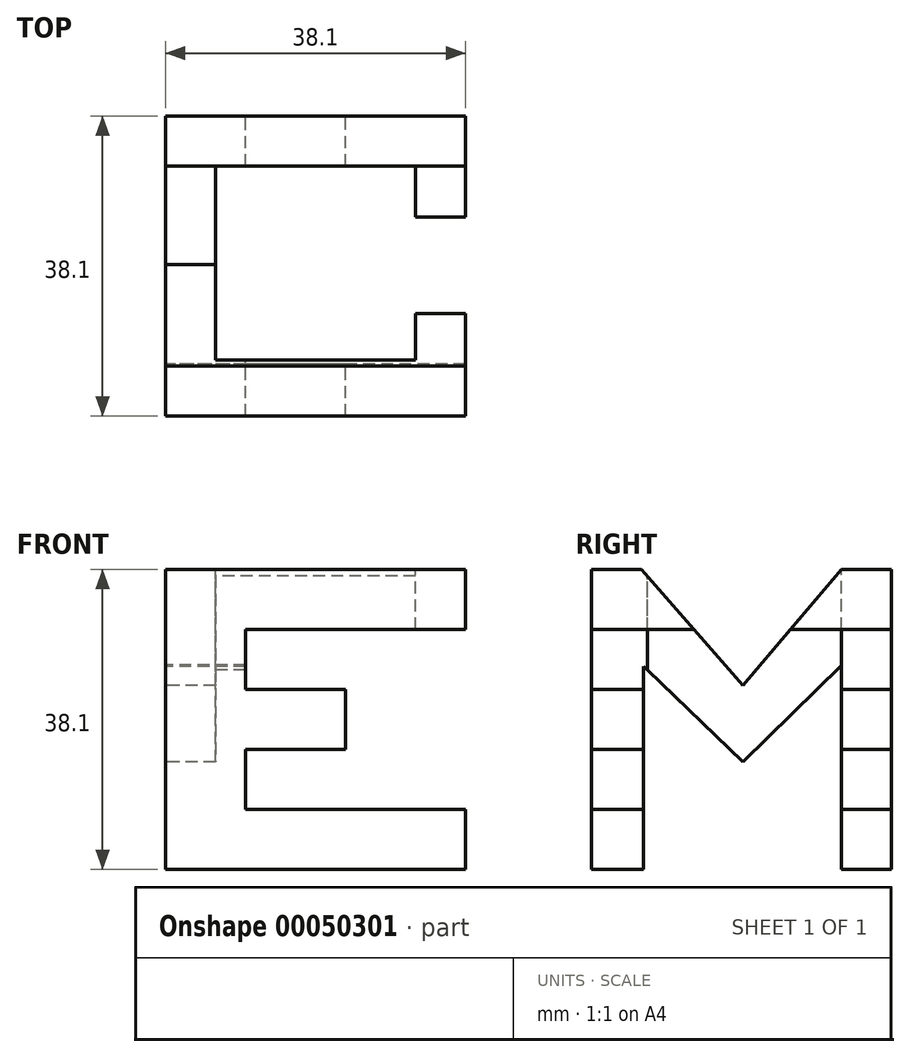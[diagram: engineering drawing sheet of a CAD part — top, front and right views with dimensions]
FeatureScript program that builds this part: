
annotation { "Feature Type Name" : "Feature", "Feature Type Description" : "" }
export const myFeature = defineFeature(function(context is Context, id is Id, definition is map)
    precondition{}
    {
        {
            var Q0;
            Q0=qCreatedBy(makeId("Front.planeOp"),FACE);
            var sketch = newSketch(context, id + "F0", { "sketchPlane" : qUnion([Q0])});
            skLineSegment(sketch, "E0.bottom", {"start": v(0, 0) * mm, "end": v(38.1, 0) * mm});
            skLineSegment(sketch, "E0.top", {"start": v(0, 38.1) * mm, "end": v(38.1, 38.1) * mm});
            skLineSegment(sketch, "E0.left", {"start": v(0, 0) * mm, "end": v(0, 38.1) * mm});
            skLineSegment(sketch, "E0.right", {"start": v(38.1, 0) * mm, "end": v(38.1, 38.1) * mm});
            skSolve(sketch);
        }
        {
            var Q0;
            Q0=qCreatedBy(makeId("Front.planeOp"),FACE);
            var sketch = newSketch(context, id + "F1", { "sketchPlane" : qUnion([Q0])});
            skSolve(sketch);
        }
        {
            var Q0;
            Q0 = qSketchRegion(id + "F1", true);
            var Q1;
            Q1=makeQuery(id+"F0.imprint","IMPRINT",FACE,{"disambiguationData":[TD([[makeQuery(id+"F0.imprint","IMPRINT",EDGE,{"derivedFrom":sQuery(id+"F0.wireOp",EDGE,"E0.bottom")}),1.0]])]});
            extrude(context, id + "F2", {"entities" : qUnion([Q0, Q1]), "depth" : 38.1 * mm});
        }
        {
            var Q0;
            Q0=qCreatedBy(makeId("Front.planeOp"),FACE);
            var sketch = newSketch(context, id + "F3", { "sketchPlane" : qUnion([Q0])});
            skLineSegment(sketch, "E1", {"start": v(0, 0) * mm, "end": v(0, 38.1) * mm});
            skLineSegment(sketch, "E2", {"start": v(0, 38.1) * mm, "end": v(38.1, 38.1) * mm});
            skLineSegment(sketch, "E3", {"start": v(38.1, 38.1) * mm, "end": v(38.1, 30.48) * mm});
            skLineSegment(sketch, "E4", {"start": v(38.1, 30.48) * mm, "end": v(10.16, 30.48) * mm});
            skLineSegment(sketch, "E5", {"start": v(10.16, 30.48) * mm, "end": v(10.16, 22.86) * mm});
            skLineSegment(sketch, "E6", {"start": v(10.16, 22.86) * mm, "end": v(22.86, 22.86) * mm});
            skLineSegment(sketch, "E7", {"start": v(22.86, 22.86) * mm, "end": v(22.86, 15.24) * mm});
            skLineSegment(sketch, "E8", {"start": v(22.86, 15.24) * mm, "end": v(10.16, 15.24) * mm});
            skLineSegment(sketch, "E9", {"start": v(10.16, 15.24) * mm, "end": v(10.16, 7.62) * mm});
            skLineSegment(sketch, "E10", {"start": v(10.16, 7.62) * mm, "end": v(38.1, 7.62) * mm});
            skLineSegment(sketch, "E11", {"start": v(38.1, 7.62) * mm, "end": v(38.1, 0) * mm});
            skLineSegment(sketch, "E12", {"start": v(38.1, 7.62) * mm, "end": v(38.1, 30.48) * mm});
            skSolve(sketch);
        }
        {
            var Q0;
            Q0=makeQuery(id+"F3.imprint","IMPRINT",FACE,{"disambiguationData":[TD([[makeQuery(id+"F3.imprint","IMPRINT",EDGE,{"derivedFrom":sQuery(id+"F3.wireOp",EDGE,"E4")}),1.0]])]});
            extrude(context, id + "F4", {"entities" : qUnion([Q0]), "operationType" : NewBodyOperationType.REMOVE, "depth" : 38.1 * mm});
        }
        {
            var Q0;
            Q0=qCreatedBy(makeId("Top.planeOp"),FACE);
            cPlane(context, id + "F5", {"entities" : qUnion([Q0]), "cplaneType" : CPlaneType.OFFSET, "offset" : 38.1 * mm, "width" : 152.4 * mm, "height" : 152.4 * mm});
        }
        {
            var Q0;
            Q0=qCreatedBy(id+"F5.planeOp",FACE);
            var sketch = newSketch(context, id + "F6", { "sketchPlane" : qUnion([Q0])});
            skLineSegment(sketch, "E13", {"start": v(0, 0) * mm, "end": v(0, -38.1) * mm});
            skLineSegment(sketch, "E14", {"start": v(0, -38.1) * mm, "end": v(38.1, -38.1) * mm});
            skLineSegment(sketch, "E15", {"start": v(38.1, -38.1) * mm, "end": v(38.1, 0) * mm});
            skLineSegment(sketch, "E16", {"start": v(0, 0) * mm, "end": v(38.1, 0) * mm});
            skLineSegment(sketch, "E17", {"start": v(6.35, -6.38) * mm, "end": v(31.75, -6.38) * mm});
            skLineSegment(sketch, "E18", {"start": v(31.75, -6.38) * mm, "end": v(31.75, -31.02) * mm});
            skLineSegment(sketch, "E19", {"start": v(31.75, -31.02) * mm, "end": v(6.35, -31.02) * mm});
            skLineSegment(sketch, "E20", {"start": v(6.35, -31.02) * mm, "end": v(6.35, -6.38) * mm});
            skSolve(sketch);
        }
        {
            var Q0;
            Q0=qCreatedBy(id+"F5.planeOp",FACE);
            var sketch = newSketch(context, id + "F7", { "sketchPlane" : qUnion([Q0])});
            skSolve(sketch);
        }
        {
            var Q0;
            Q0 = qSketchRegion(id + "F7", true);
            var Q1;
            Q1=makeQuery(id+"F6.imprint","IMPRINT",FACE,{"disambiguationData":[TD([[makeQuery(id+"F6.imprint","IMPRINT",EDGE,{"derivedFrom":sQuery(id+"F6.wireOp",EDGE,"E17")}),-1.0]])]});
            extrude(context, id + "F8", {"entities" : qUnion([Q0, Q1]), "operationType" : NewBodyOperationType.REMOVE, "oppositeDirection" : true, "depth" : 38.1 * mm});
        }
        {
            var Q0;
            Q0=qCreatedBy(makeId("Right.planeOp"),FACE);
            var sketch = newSketch(context, id + "F9", { "sketchPlane" : qUnion([Q0])});
            skLineSegment(sketch, "E21", {"start": v(0, 0) * mm, "end": v(-6.35, 0) * mm});
            skLineSegment(sketch, "E22", {"start": v(-6.35, 0) * mm, "end": v(-6.35, 21.6) * mm});
            skLineSegment(sketch, "E23", {"start": v(-6.35, 21.6) * mm, "end": v(-18.86, 10.86) * mm});
            skLineSegment(sketch, "E24", {"start": v(-18.86, 10.86) * mm, "end": v(-31.78, 21.63) * mm});
            skLineSegment(sketch, "E25", {"start": v(-31.78, 21.63) * mm, "end": v(-31.78, 0) * mm});
            skLineSegment(sketch, "E26", {"start": v(-6.35, 38.1) * mm, "end": v(-18.86, 23.38) * mm});
            skLineSegment(sketch, "E27", {"start": v(-18.86, 23.38) * mm, "end": v(-31.78, 38.15) * mm});
            skLineSegment(sketch, "E28", {"start": v(-6.35, 38.1) * mm, "end": v(0, 38.1) * mm});
            skLineSegment(sketch, "E29", {"start": v(0, 38.1) * mm, "end": v(0, 0) * mm});
            skLineSegment(sketch, "E30", {"start": v(-38.13, 0) * mm, "end": v(-38.13, 38.1) * mm});
            skLineSegment(sketch, "E31", {"start": v(-38.13, 38.1) * mm, "end": v(-6.35, 38.1) * mm});
            skLineSegment(sketch, "E32", {"start": v(-38.13, 38.1) * mm, "end": v(-31.78, 38.15) * mm});
            skLineSegment(sketch, "E33", {"start": v(-31.78, 0) * mm, "end": v(-38.13, 0) * mm});
            skLineSegment(sketch, "E34", {"start": v(0, 38.1) * mm, "end": v(-38.13, 38.1) * mm});
            skLineSegment(sketch, "E35", {"start": v(-6.35, 0) * mm, "end": v(-31.78, 0) * mm});
            skSolve(sketch);
        }
        {
            var Q0;
            {var subQ0=sQuery(id+"F9.wireOp",EDGE,"E26");Q0=makeQuery(id+"F9.imprint","IMPRINT",FACE,{"disambiguationData":[TD([[makeQuery(id+"F9.imprint","IMPRINT",EDGE,{"derivedFrom":subQ0}),-1.0]])]});}
            extrude(context, id + "F10", {"entities" : qUnion([Q0]), "operationType" : NewBodyOperationType.REMOVE, "depth" : 38.1 * mm});
        }
        {
            var Q0;
            Q0=qCreatedBy(makeId("Right.planeOp"),FACE);
            var sketch = newSketch(context, id + "F11", { "sketchPlane" : qUnion([Q0])});
            skLineSegment(sketch, "E36", {"start": v(-6.35, 0) * mm, "end": v(-6.35, 25.96) * mm});
            skLineSegment(sketch, "E37", {"start": v(-6.35, 25.96) * mm, "end": v(-18.89, 13.65) * mm});
            skLineSegment(sketch, "E38", {"start": v(-18.89, 13.65) * mm, "end": v(-31.5, 25.79) * mm});
            skLineSegment(sketch, "E39", {"start": v(-31.5, 25.79) * mm, "end": v(-31.5, 0) * mm});
            skLineSegment(sketch, "E40", {"start": v(-6.35, 0) * mm, "end": v(0, 0) * mm});
            skLineSegment(sketch, "E41", {"start": v(-6.35, 0) * mm, "end": v(-31.5, 0) * mm});
            skLineSegment(sketch, "E42", {"start": v(0, 0) * mm, "end": v(-6.35, 0) * mm});
            skLineSegment(sketch, "E43", {"start": v(-31.5, 0) * mm, "end": v(-37.85, 0) * mm});
            skLineSegment(sketch, "E44", {"start": v(-37.85, 0) * mm, "end": v(-37.85, 38.1) * mm});
            skSolve(sketch);
        }
        {
            var Q0;
            Q0 = qSketchRegion(id + "F11", true);
            extrude(context, id + "F12", {"entities" : qUnion([Q0]), "operationType" : NewBodyOperationType.REMOVE, "depth" : 38.1 * mm});
        }
    });
